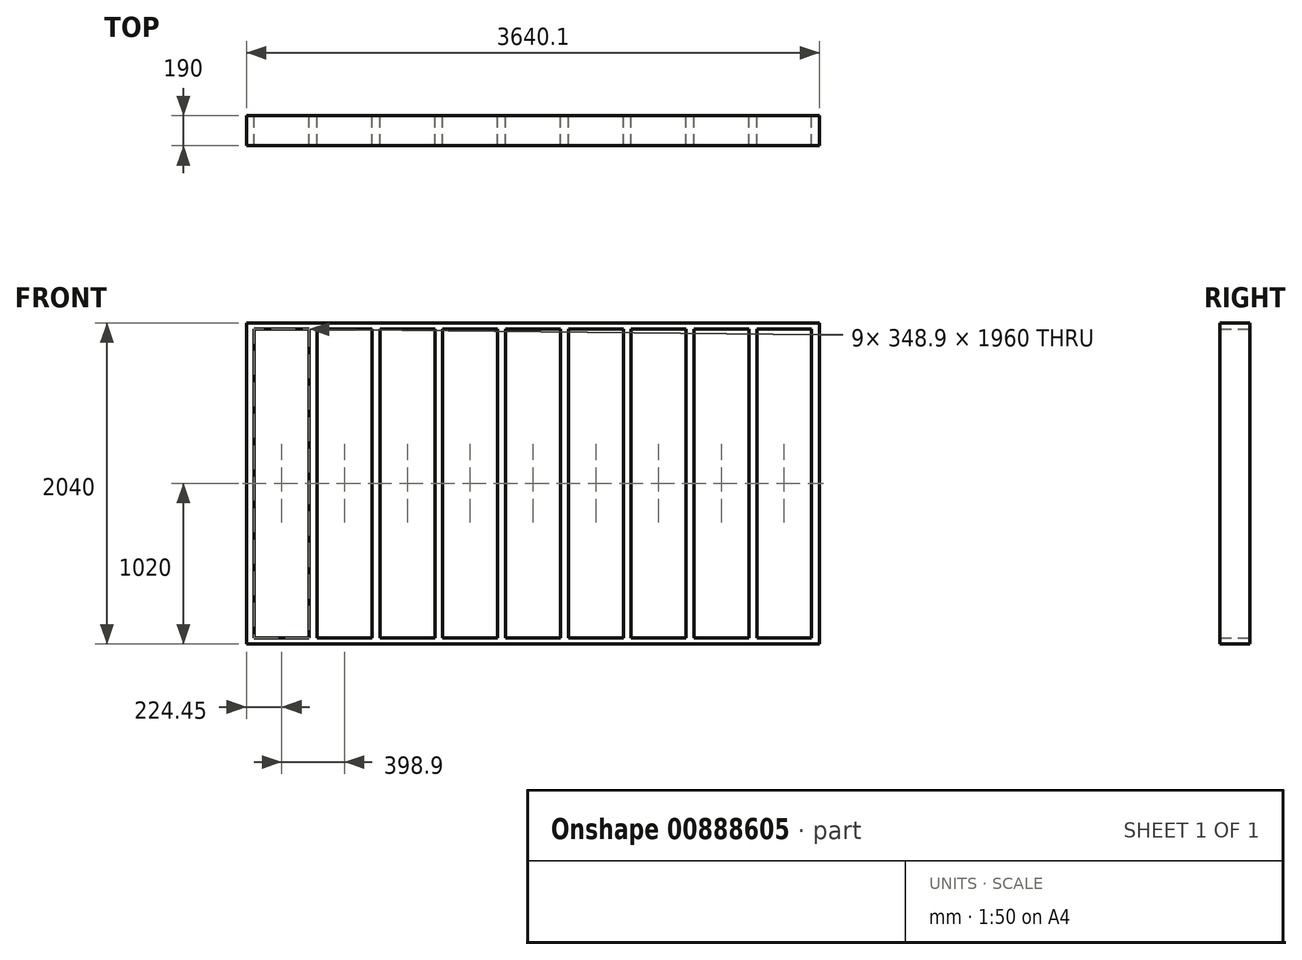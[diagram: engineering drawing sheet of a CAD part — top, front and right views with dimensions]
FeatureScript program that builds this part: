
annotation { "Feature Type Name" : "Feature", "Feature Type Description" : "" }
export const myFeature = defineFeature(function(context is Context, id is Id, definition is map)
    precondition{}
    {
        {
            var Q0;
            Q0=qCreatedBy(makeId("Front.planeOp"),FACE);
            var sketch = newSketch(context, id + "F0", { "sketchPlane" : qUnion([Q0])});
            skLineSegment(sketch, "E0.bottom", {"start": v(-1820, 0) * mm, "end": v(1820, 0) * mm});
            skLineSegment(sketch, "E0.top", {"start": v(-1820, 40) * mm, "end": v(1820, 40) * mm});
            skLineSegment(sketch, "E0.left", {"start": v(-1820, 0) * mm, "end": v(-1820, 40) * mm});
            skLineSegment(sketch, "E0.right", {"start": v(1820, 0) * mm, "end": v(1820, 40) * mm});
            skPoint(sketch, "E1", {"position": v(0, 0) * mm});
            skLineSegment(sketch, "E2.bottom", {"start": v(1820, 2040) * mm, "end": v(-1820, 2040) * mm});
            skLineSegment(sketch, "E2.top", {"start": v(1820, 2000) * mm, "end": v(-1820, 2000) * mm});
            skLineSegment(sketch, "E2.left", {"start": v(1820, 2040) * mm, "end": v(1820, 2000) * mm});
            skLineSegment(sketch, "E2.right", {"start": v(-1820, 2040) * mm, "end": v(-1820, 2000) * mm});
            skSolve(sketch);
        }
        {
            var Q0;
            Q0=makeQuery(id+"F0.imprint","IMPRINT",FACE,{"disambiguationData":[TD([[makeQuery(id+"F0.imprint","IMPRINT",EDGE,{"derivedFrom":sQuery(id+"F0.wireOp",EDGE,"E0.bottom")}),1.0]])]});
            extrude(context, id + "F1", {"entities" : qUnion([Q0]), "depth" : 190 * mm, "offsetDistance" : 25 * mm});
        }
        {
            var Q0;
            Q0=makeQuery(id+"F0.imprint","IMPRINT",FACE,{"disambiguationData":[TD([[makeQuery(id+"F0.imprint","IMPRINT",EDGE,{"derivedFrom":sQuery(id+"F0.wireOp",EDGE,"E2.bottom")}),1.0]])]});
            extrude(context, id + "F2", {"entities" : qUnion([Q0]), "depth" : 190 * mm, "offsetDistance" : 25 * mm});
        }
        {
            var Q0;
            Q0=qCreatedBy(makeId("Front.planeOp"),FACE);
            var sketch = newSketch(context, id + "F3", { "sketchPlane" : qUnion([Q0])});
            skLineSegment(sketch, "E3.bottom", {"start": v(1820, 2000) * mm, "end": v(1770, 2000) * mm});
            skLineSegment(sketch, "E3.top", {"start": v(1820, 40) * mm, "end": v(1770, 40) * mm});
            skLineSegment(sketch, "E3.left", {"start": v(1820, 2000) * mm, "end": v(1820, 40) * mm});
            skLineSegment(sketch, "E3.right", {"start": v(1770, 2000) * mm, "end": v(1770, 40) * mm});
            skLineSegment(sketch, "E4.1.0.0", {"start": v(1371.1, 2000) * mm, "end": v(1371.1, 40) * mm});
            skLineSegment(sketch, "E4.1.0.1", {"start": v(1421.1, 2000) * mm, "end": v(1421.1, 40) * mm});
            skLineSegment(sketch, "E4.1.0.2", {"start": v(1421.1, 2000) * mm, "end": v(1371.1, 2000) * mm});
            skLineSegment(sketch, "E4.1.0.3", {"start": v(1421.1, 40) * mm, "end": v(1371.1, 40) * mm});
            skLineSegment(sketch, "E4.2.0.0", {"start": v(972.2, 2000) * mm, "end": v(972.2, 40) * mm});
            skLineSegment(sketch, "E4.2.0.1", {"start": v(1022.2, 2000) * mm, "end": v(1022.2, 40) * mm});
            skLineSegment(sketch, "E4.2.0.2", {"start": v(1022.2, 2000) * mm, "end": v(972.2, 2000) * mm});
            skLineSegment(sketch, "E4.2.0.3", {"start": v(1022.2, 40) * mm, "end": v(972.2, 40) * mm});
            skLineSegment(sketch, "E4.3.0.0", {"start": v(573.3, 2000) * mm, "end": v(573.3, 40) * mm});
            skLineSegment(sketch, "E4.3.0.1", {"start": v(623.3, 2000) * mm, "end": v(623.3, 40) * mm});
            skLineSegment(sketch, "E4.3.0.2", {"start": v(623.3, 2000) * mm, "end": v(573.3, 2000) * mm});
            skLineSegment(sketch, "E4.3.0.3", {"start": v(623.3, 40) * mm, "end": v(573.3, 40) * mm});
            skLineSegment(sketch, "E4.4.0.0", {"start": v(174.4, 2000) * mm, "end": v(174.4, 40) * mm});
            skLineSegment(sketch, "E4.4.0.1", {"start": v(224.4, 2000) * mm, "end": v(224.4, 40) * mm});
            skLineSegment(sketch, "E4.4.0.2", {"start": v(224.4, 2000) * mm, "end": v(174.4, 2000) * mm});
            skLineSegment(sketch, "E4.4.0.3", {"start": v(224.4, 40) * mm, "end": v(174.4, 40) * mm});
            skLineSegment(sketch, "E4.5.0.0", {"start": v(-224.5, 2000) * mm, "end": v(-224.5, 40) * mm});
            skLineSegment(sketch, "E4.5.0.1", {"start": v(-174.5, 2000) * mm, "end": v(-174.5, 40) * mm});
            skLineSegment(sketch, "E4.5.0.2", {"start": v(-174.5, 2000) * mm, "end": v(-224.5, 2000) * mm});
            skLineSegment(sketch, "E4.5.0.3", {"start": v(-174.5, 40) * mm, "end": v(-224.5, 40) * mm});
            skLineSegment(sketch, "E4.6.0.0", {"start": v(-623.4, 2000) * mm, "end": v(-623.4, 40) * mm});
            skLineSegment(sketch, "E4.6.0.1", {"start": v(-573.4, 2000) * mm, "end": v(-573.4, 40) * mm});
            skLineSegment(sketch, "E4.6.0.2", {"start": v(-573.4, 2000) * mm, "end": v(-623.4, 2000) * mm});
            skLineSegment(sketch, "E4.6.0.3", {"start": v(-573.4, 40) * mm, "end": v(-623.4, 40) * mm});
            skLineSegment(sketch, "E4.7.0.0", {"start": v(-1022.3, 2000) * mm, "end": v(-1022.3, 40) * mm});
            skLineSegment(sketch, "E4.7.0.1", {"start": v(-972.3, 2000) * mm, "end": v(-972.3, 40) * mm});
            skLineSegment(sketch, "E4.7.0.2", {"start": v(-972.3, 2000) * mm, "end": v(-1022.3, 2000) * mm});
            skLineSegment(sketch, "E4.7.0.3", {"start": v(-972.3, 40) * mm, "end": v(-1022.3, 40) * mm});
            skLineSegment(sketch, "E4.8.0.0", {"start": v(-1421.2, 2000) * mm, "end": v(-1421.2, 40) * mm});
            skLineSegment(sketch, "E4.8.0.1", {"start": v(-1371.2, 2000) * mm, "end": v(-1371.2, 40) * mm});
            skLineSegment(sketch, "E4.8.0.2", {"start": v(-1371.2, 2000) * mm, "end": v(-1421.2, 2000) * mm});
            skLineSegment(sketch, "E4.8.0.3", {"start": v(-1371.2, 40) * mm, "end": v(-1421.2, 40) * mm});
            skLineSegment(sketch, "E4.9.0.0", {"start": v(-1820.1, 2000) * mm, "end": v(-1820.1, 40) * mm});
            skLineSegment(sketch, "E4.9.0.1", {"start": v(-1770.1, 2000) * mm, "end": v(-1770.1, 40) * mm});
            skLineSegment(sketch, "E4.9.0.2", {"start": v(-1770.1, 2000) * mm, "end": v(-1820.1, 2000) * mm});
            skLineSegment(sketch, "E4.9.0.3", {"start": v(-1770.1, 40) * mm, "end": v(-1820.1, 40) * mm});
            skLineSegment(sketch, "E4.direction1", {"start": v(1770, 40) * mm, "end": v(1371.1, 40) * mm, "construction": true});
            skSolve(sketch);
        }
        {
            var Q0;
            Q0=makeQuery(id+"F3.imprint","IMPRINT",FACE,{"disambiguationData":[TD([[makeQuery(id+"F3.imprint","IMPRINT",EDGE,{"derivedFrom":sQuery(id+"F3.wireOp",EDGE,"E3.bottom")}),1.0]])]});
            var Q1;
            Q1=makeQuery(id+"F3.imprint","IMPRINT",FACE,{"disambiguationData":[TD([[makeQuery(id+"F3.imprint","IMPRINT",EDGE,{"derivedFrom":sQuery(id+"F3.wireOp",EDGE,"E4.1.0.0")}),1.0]])]});
            var Q2;
            Q2=makeQuery(id+"F3.imprint","IMPRINT",FACE,{"disambiguationData":[TD([[makeQuery(id+"F3.imprint","IMPRINT",EDGE,{"derivedFrom":sQuery(id+"F3.wireOp",EDGE,"E4.2.0.0")}),1.0]])]});
            var Q3;
            Q3=makeQuery(id+"F3.imprint","IMPRINT",FACE,{"disambiguationData":[TD([[makeQuery(id+"F3.imprint","IMPRINT",EDGE,{"derivedFrom":sQuery(id+"F3.wireOp",EDGE,"E4.3.0.0")}),1.0]])]});
            var Q4;
            Q4=makeQuery(id+"F3.imprint","IMPRINT",FACE,{"disambiguationData":[TD([[makeQuery(id+"F3.imprint","IMPRINT",EDGE,{"derivedFrom":sQuery(id+"F3.wireOp",EDGE,"E4.4.0.0")}),1.0]])]});
            var Q5;
            Q5=makeQuery(id+"F3.imprint","IMPRINT",FACE,{"disambiguationData":[TD([[makeQuery(id+"F3.imprint","IMPRINT",EDGE,{"derivedFrom":sQuery(id+"F3.wireOp",EDGE,"E4.5.0.0")}),1.0]])]});
            var Q6;
            Q6=makeQuery(id+"F3.imprint","IMPRINT",FACE,{"disambiguationData":[TD([[makeQuery(id+"F3.imprint","IMPRINT",EDGE,{"derivedFrom":sQuery(id+"F3.wireOp",EDGE,"E4.6.0.0")}),1.0]])]});
            var Q7;
            Q7=makeQuery(id+"F3.imprint","IMPRINT",FACE,{"disambiguationData":[TD([[makeQuery(id+"F3.imprint","IMPRINT",EDGE,{"derivedFrom":sQuery(id+"F3.wireOp",EDGE,"E4.7.0.0")}),1.0]])]});
            var Q8;
            Q8=makeQuery(id+"F3.imprint","IMPRINT",FACE,{"disambiguationData":[TD([[makeQuery(id+"F3.imprint","IMPRINT",EDGE,{"derivedFrom":sQuery(id+"F3.wireOp",EDGE,"E4.8.0.0")}),1.0]])]});
            var Q9;
            Q9=makeQuery(id+"F3.imprint","IMPRINT",FACE,{"disambiguationData":[TD([[makeQuery(id+"F3.imprint","IMPRINT",EDGE,{"derivedFrom":sQuery(id+"F3.wireOp",EDGE,"E4.9.0.0")}),1.0]])]});
            extrude(context, id + "F4", {"entities" : qUnion([Q0, Q1, Q2, Q3, Q4, Q5, Q6, Q7, Q8, Q9]), "operationType" : NewBodyOperationType.ADD, "depth" : 190 * mm, "offsetDistance" : 25 * mm});
        }
    });
